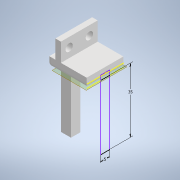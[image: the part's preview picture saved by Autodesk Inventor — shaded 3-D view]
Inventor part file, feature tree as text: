
AUTODESK INVENTOR PART (.ipt)
format: ipt  version: 2021 (Build 250183000, 183)  size: 192,000 bytes
history: native  units: mm
features: sketch x10, reference x8, extrude x7, other x7, projected_geometry x3, fillet x2, plane x1, split x1, direct_edit x1, move_body x1
ambient origin geometry x8: Origin, YZ Plane, XZ Plane, XY Plane, X Axis, Y Axis, Z Axis, Center Point
bodies: Solid1 (feature_tree)
feature tree (41):
  extrude  "Extrusion1"  Depth=20.0mm
  extrude  "Extrusion3"  Depth=5.0mm
  extrude  "Extrusion4"  Depth=3.0mm
  extrude  "Extrusion5"  Depth=5.0mm TaperAngle=0.0deg
  extrude  "Extrusion6"  Depth=5.0mm TaperAngle=0.0deg
  plane  "Work Plane1"
  split  "Split1"
  extrude  "Extrusion7"  TaperAngle=0.0deg  [1 undecoded]
  extrude  "Extrusion8"  Depth=4.0mm TaperAngle=0.0deg
  direct_edit  "Direct Edit1"
  fillet  "Fillet3"  Radius=2.0mm
  fillet  "Fillet4"  Radius=2.0mm
  sketch  "Sketch11"
  sketch  "Sketch2"  dims[d2=17.0mm d3=0.0mm d4=5.0mm]
  sketch  "Sketch12"
  sketch  "Sketch1"  dims[d0=5.0mm d1=20.0mm]
  sketch  "Sketch3"  dims[d5=35.0mm d8=3.0mm]
  sketch  "Sketch4"  dims[d9=10.0mm d10=5.0mm d11=0.0mm]
  reference  "Reference1"
  reference  "Reference2"
  sketch  "Sketch5"  dims[d12=5.0mm d13=0.0mm d14=5.0mm d15=0.0mm]
  reference  "Reference3"
  reference  "Reference4"
  reference  "Reference5"
  reference  "Reference6"
  sketch  "Sketch6"  dims[d16=10.0mm d17=0.0mm d18=0.0mm]
  reference  "Reference7"
  reference  "Reference8"
  sketch  "Sketch7"  dims[d19=4.0mm d20=0.0mm d21=4.0mm d22=0.0mm]
  projected_geometry  "Projected Loop1"
  projected_geometry  "Projected Loop2"
  sketch  "Sketch8"  dims[d27=0.0mm d28=0.0mm d29=0.5mm d31=2.0mm d32=2.0mm]
  projected_geometry  "Projected Loop3"
  parser-record x3  (decoder bookkeeping rows leaked as tree rows — omitted from the tree; the rows remain in map.json)
  other  "whole_assembly.iam"
  other  "normal_finger:1"
  other  "reverse_finger:2"
  other  "normal_finger:2"
  move_body  "Move1"
note: 1 required parameter value undecoded (feature->parameter linkage not recoverable at this tier; creation-order binding heuristic only, values carry confidence <= 0.55)
note: 3 file-system paths scrubbed to <path> (originals preserved in map.json)
